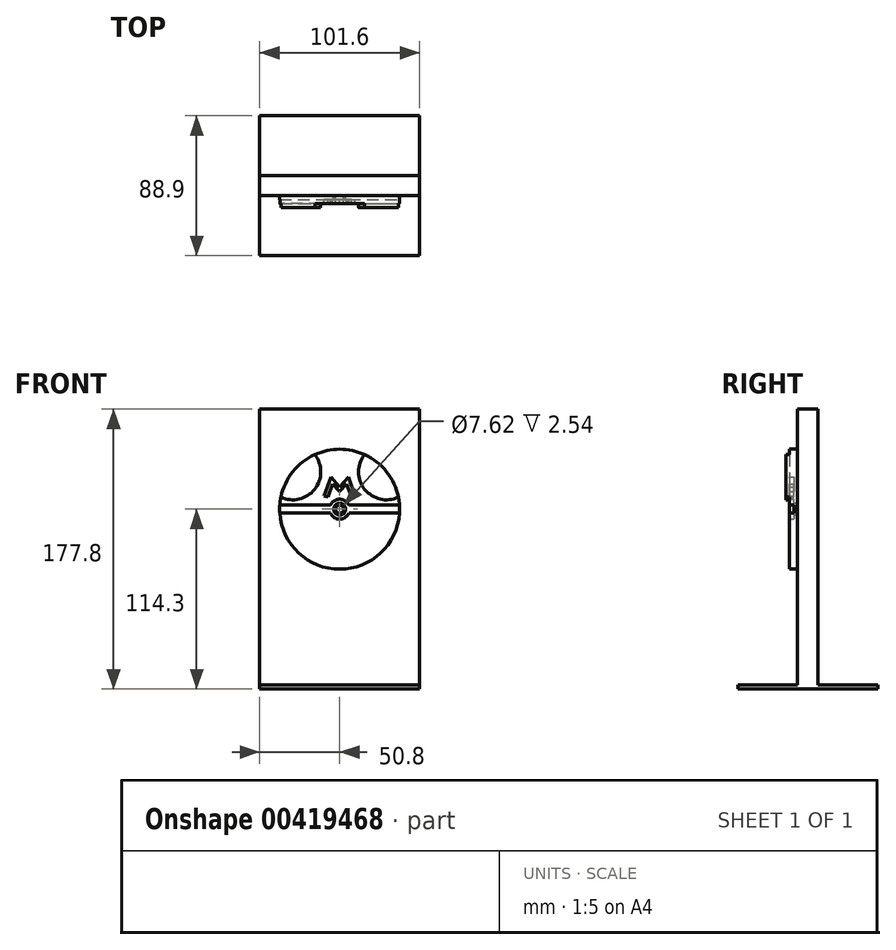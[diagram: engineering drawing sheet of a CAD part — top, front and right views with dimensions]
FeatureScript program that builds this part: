
annotation { "Feature Type Name" : "Feature", "Feature Type Description" : "" }
export const myFeature = defineFeature(function(context is Context, id is Id, definition is map)
    precondition{}
    {
        {
            var Q0;
            Q0=qCreatedBy(makeId("Front.planeOp"),FACE);
            var sketch = newSketch(context, id + "F0", { "sketchPlane" : qUnion([Q0])});
            skLineSegment(sketch, "E0.bottom", {"start": v(0, 0) * mm, "end": v(101.6, 0) * mm});
            skLineSegment(sketch, "E0.top", {"start": v(0, 177.8) * mm, "end": v(101.6, 177.8) * mm});
            skLineSegment(sketch, "E0.left", {"start": v(0, 0) * mm, "end": v(0, 177.8) * mm});
            skLineSegment(sketch, "E0.right", {"start": v(101.6, 0) * mm, "end": v(101.6, 177.8) * mm});
            skLineSegment(sketch, "E1.top", {"start": v(0, 2.54) * mm, "end": v(101.6, 2.54) * mm});
            skLineSegment(sketch, "E1.left", {"start": v(0, 0) * mm, "end": v(0, 2.54) * mm});
            skLineSegment(sketch, "E1.right", {"start": v(101.6, 0) * mm, "end": v(101.6, 2.54) * mm});
            skSolve(sketch);
        }
        {
            var Q0;
            Q0=makeQuery(id+"F0.imprint","IMPRINT",FACE,{"disambiguationData":[TD([[makeQuery(id+"F0.imprint","IMPRINT",EDGE,{"derivedFrom":sQuery(id+"F0.wireOp",EDGE,"E0.top")}),-1.0]])]});
            extrude(context, id + "F1", {"entities" : qUnion([Q0]), "depth" : 12.7 * mm});
        }
        {
            var Q0;
            Q0=makeQuery(id+"F0.imprint","IMPRINT",FACE,{"disambiguationData":[TD([[makeQuery(id+"F0.imprint","IMPRINT",EDGE,{"derivedFrom":sQuery(id+"F0.wireOp",EDGE,"E0.bottom")}),1.0]])]});
            var Q1;
            {var subQ0=sQuery(id+"F0.wireOp",EDGE,"E1.top");Q1=makeQuery(id+"F0.imprint","IMPRINT",FACE,{"disambiguationData":[TD([[makeQuery(id+"F0.imprint","IMPRINT",EDGE,{"derivedFrom":subQ0}),-1.0]])]});}
            extrude(context, id + "F2", {"entities" : qUnion([Q0, Q1]), "operationType" : NewBodyOperationType.ADD, "depth" : 50.8 * mm, "hasSecondDirection" : true, "secondDirectionOppositeDirection" : true, "secondDirectionDepth" : 38.1 * mm});
        }
        {
            var Q0;
            Q0=makeQuery(id+"F1.opExtrude","CAP_FACE",FACE,{"disambiguationData":[OSD([sQuery(id+"F0.wireOp",EDGE,"E0.top"),sQuery(id+"F0.wireOp",EDGE,"E0.left"),sQuery(id+"F0.wireOp",EDGE,"E0.right"),sQuery(id+"F0.wireOp",EDGE,"E1.top")])],"isStart":false});
            var sketch = newSketch(context, id + "F3", { "sketchPlane" : qUnion([Q0])});
            skCircle(sketch, "E2", {"center": v(50.8, 114.3) * mm, "radius": 38.1 * mm});
            skCircle(sketch, "E3", {"center": v(50.8, 114.3) * mm, "radius": 6.35 * mm});
            skCircle(sketch, "E4", {"center": v(50.8, 114.3) * mm, "radius": 3.81 * mm});
            skCircle(sketch, "E5", {"center": v(50.8, 114.3) * mm, "radius": 2.54 * mm});
            skLineSegment(sketch, "E6", {"start": v(12.78, 116.84) * mm, "end": v(44.98, 116.84) * mm});
            skLineSegment(sketch, "E7", {"start": v(44.98, 111.76) * mm, "end": v(12.78, 111.76) * mm});
            skLineSegment(sketch, "E8", {"start": v(56.62, 116.84) * mm, "end": v(88.82, 116.84) * mm});
            skLineSegment(sketch, "E9", {"start": v(56.62, 111.76) * mm, "end": v(88.82, 111.76) * mm});
            skArc(sketch, "E10", {"start": v(13.47, 121.92) * mm, "mid": v(34.9, 126.96) * mm, "end": v(35, 148.97) * mm});
            skArc(sketch, "E11", {"start": v(66.6, 148.97) * mm, "mid": v(66.7, 126.96) * mm, "end": v(88.13, 121.92) * mm});
            skLineSegment(sketch, "E12", {"start": v(40.9, 122.68) * mm, "end": v(45.24, 134.62) * mm});
            skLineSegment(sketch, "E13", {"start": v(45.24, 134.62) * mm, "end": v(50.8, 128.52) * mm});
            skLineSegment(sketch, "E14", {"start": v(50.8, 128.52) * mm, "end": v(56.36, 134.62) * mm});
            skLineSegment(sketch, "E15", {"start": v(56.36, 134.62) * mm, "end": v(60.7, 122.68) * mm});
            skLineSegment(sketch, "E16", {"start": v(58.28, 121.94) * mm, "end": v(60.7, 122.68) * mm});
            skLineSegment(sketch, "E17", {"start": v(58.28, 121.94) * mm, "end": v(55.24, 130.3) * mm});
            skLineSegment(sketch, "E18", {"start": v(55.24, 130.3) * mm, "end": v(50.8, 125.48) * mm});
            skLineSegment(sketch, "E19", {"start": v(50.8, 125.48) * mm, "end": v(46.36, 130.3) * mm});
            skLineSegment(sketch, "E20", {"start": v(46.36, 130.3) * mm, "end": v(43.32, 121.94) * mm});
            skLineSegment(sketch, "E21", {"start": v(43.32, 121.94) * mm, "end": v(40.9, 122.68) * mm});
            skLineSegment(sketch, "E22", {"start": v(50.8, 114.3) * mm, "end": v(50.8, 152.4) * mm, "construction": true});
            skArc(sketch, "E23", {"start": v(38.74, 147.92) * mm, "mid": v(15.55, 142.77) * mm, "end": v(14.6, 119.04) * mm});
            skArc(sketch, "E24", {"start": v(86.32, 118.66) * mm, "mid": v(86.64, 143.33) * mm, "end": v(62.45, 148.18) * mm});
            skSolve(sketch);
        }
        {
            var Q0;
            {var subQ0=sQuery(id+"F3.wireOp",EDGE,"E11");Q0=makeQuery(id+"F3.imprint","IMPRINT",FACE,{"disambiguationData":[TD([[makeQuery(id+"F3.imprint","IMPRINT",EDGE,{"derivedFrom":subQ0}),1.0]])]});}
            var Q1;
            {var subQ0=sQuery(id+"F3.wireOp",EDGE,"E10");Q1=makeQuery(id+"F3.imprint","IMPRINT",FACE,{"disambiguationData":[TD([[makeQuery(id+"F3.imprint","IMPRINT",EDGE,{"derivedFrom":subQ0}),1.0]])]});}
            extrude(context, id + "F4", {"entities" : qUnion([Q0, Q1]), "operationType" : NewBodyOperationType.ADD, "depth" : 7.62 * mm});
        }
        {
            var Q0;
            {var subQ0=sQuery(id+"F3.wireOp",EDGE,"E7");Q0=makeQuery(id+"F3.imprint","IMPRINT",FACE,{"disambiguationData":[TD([[makeQuery(id+"F3.imprint","IMPRINT",EDGE,{"derivedFrom":subQ0}),1.0]])]});}
            var Q1;
            {var subQ4=sQuery(id+"F3.wireOp",EDGE,"E6");Q1=makeQuery(id+"F3.imprint","IMPRINT",FACE,{"disambiguationData":[TD([[makeQuery(id+"F3.imprint","IMPRINT",EDGE,{"derivedFrom":subQ4}),1.0]])]});}
            var Q2;
            Q2=makeQuery(id+"F3.imprint","IMPRINT",FACE,{"disambiguationData":[TD([[makeQuery(id+"F3.imprint","IMPRINT",EDGE,{"derivedFrom":sQuery(id+"F3.wireOp",EDGE,"E5")}),1.0]])]});
            extrude(context, id + "F5", {"entities" : qUnion([Q0, Q1, Q2]), "operationType" : NewBodyOperationType.ADD, "depth" : 5.08 * mm});
        }
        {
            var Q0;
            {var subQ0=sQuery(id+"F3.wireOp",EDGE,"E6");Q0=makeQuery(id+"F3.imprint","IMPRINT",FACE,{"disambiguationData":[TD([[makeQuery(id+"F3.imprint","IMPRINT",EDGE,{"derivedFrom":subQ0}),-1.0]])]});}
            var Q1;
            Q1=makeQuery(id+"F3.imprint","IMPRINT",FACE,{"disambiguationData":[TD([[makeQuery(id+"F3.imprint","IMPRINT",EDGE,{"derivedFrom":sQuery(id+"F3.wireOp",EDGE,"E4")}),-1.0]])]});
            var Q2;
            {var subQ0=sQuery(id+"F3.wireOp",EDGE,"E8");Q2=makeQuery(id+"F3.imprint","IMPRINT",FACE,{"disambiguationData":[TD([[makeQuery(id+"F3.imprint","IMPRINT",EDGE,{"derivedFrom":subQ0}),-1.0]])]});}
            var Q3;
            Q3=makeQuery(id+"F3.imprint","IMPRINT",FACE,{"disambiguationData":[TD([[makeQuery(id+"F3.imprint","IMPRINT",EDGE,{"derivedFrom":sQuery(id+"F3.wireOp",EDGE,"E12")}),-1.0]])]});
            extrude(context, id + "F6", {"entities" : qUnion([Q0, Q1, Q2, Q3]), "operationType" : NewBodyOperationType.ADD, "depth" : 2.54 * mm});
        }
    });
